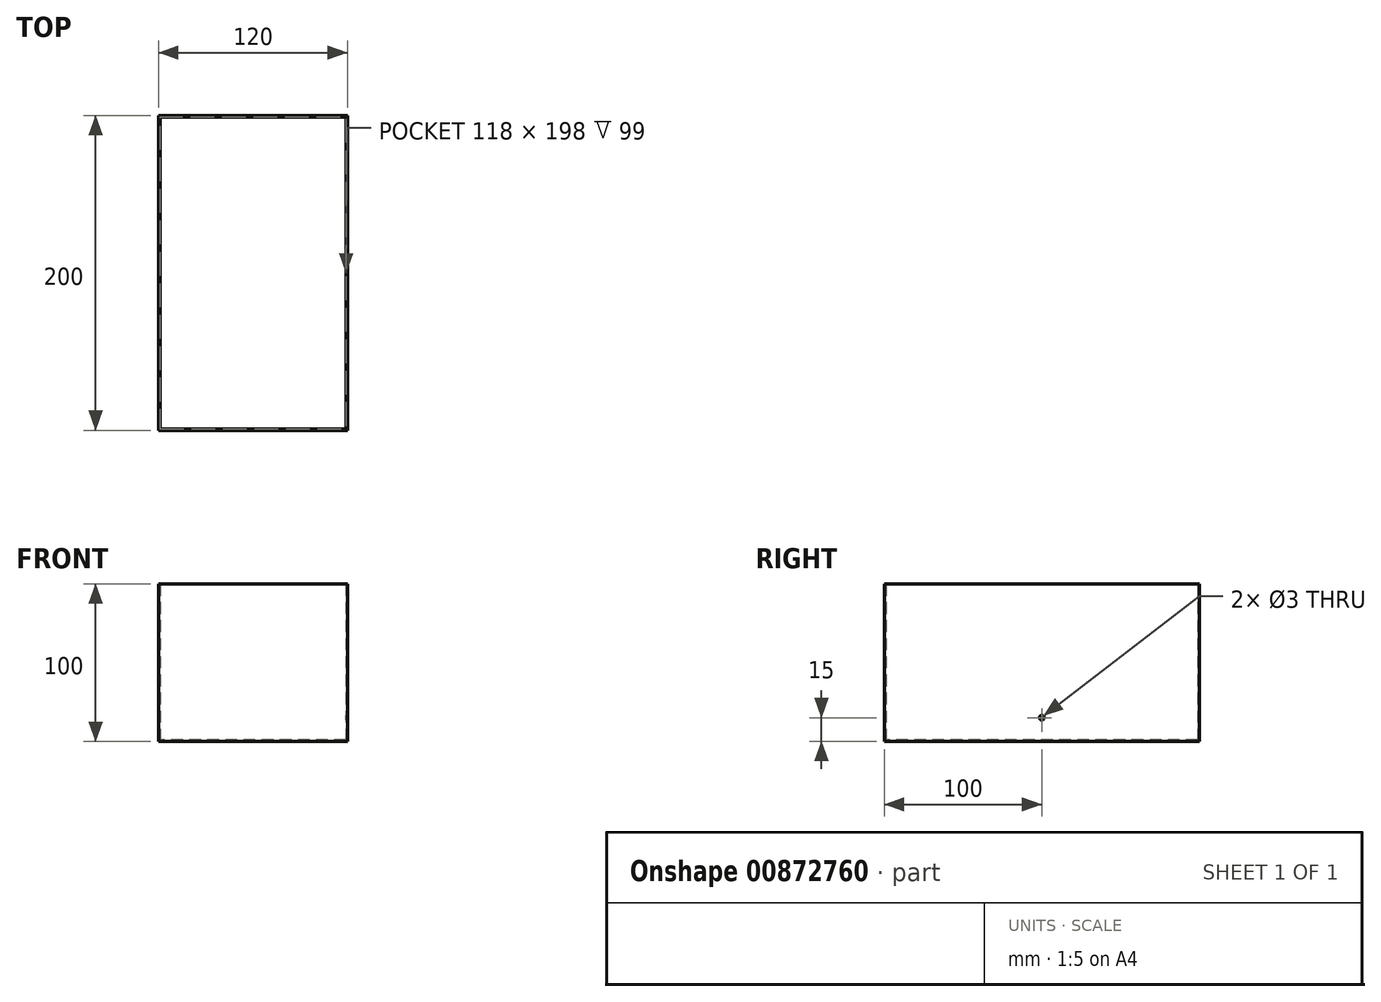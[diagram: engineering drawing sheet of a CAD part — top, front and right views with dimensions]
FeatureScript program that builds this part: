
annotation { "Feature Type Name" : "Feature", "Feature Type Description" : "" }
export const myFeature = defineFeature(function(context is Context, id is Id, definition is map)
    precondition{}
    {
        {
            var Q0;
            Q0=qCreatedBy(makeId("Top.planeOp"),FACE);
            var sketch = newSketch(context, id + "F0", { "sketchPlane" : qUnion([Q0])});
            skLineSegment(sketch, "E0.bottom", {"start": v(60, 100) * mm, "end": v(-60, 100) * mm});
            skLineSegment(sketch, "E0.top", {"start": v(60, -100) * mm, "end": v(-60, -100) * mm});
            skLineSegment(sketch, "E0.left", {"start": v(60, 100) * mm, "end": v(60, -100) * mm});
            skLineSegment(sketch, "E0.right", {"start": v(-60, 100) * mm, "end": v(-60, -100) * mm});
            skPoint(sketch, "E0.middle", {"position": v(0, 0) * mm});
            skSolve(sketch);
        }
        {
            var Q0;
            Q0=makeQuery(id+"F0.imprint","IMPRINT",FACE,{"disambiguationData":[TD([[makeQuery(id+"F0.imprint","IMPRINT",EDGE,{"derivedFrom":sQuery(id+"F0.wireOp",EDGE,"E0.bottom")}),1.0]])]});
            extrude(context, id + "F1", {"entities" : qUnion([Q0]), "depth" : 100 * mm, "offsetDistance" : 25 * mm});
        }
        {
            var Q0;
            Q0=makeQuery(id+"F1.opExtrude","CAP_FACE",FACE,{"disambiguationData":[OSD([sQuery(id+"F0.wireOp",EDGE,"E0.bottom"),sQuery(id+"F0.wireOp",EDGE,"E0.top"),sQuery(id+"F0.wireOp",EDGE,"E0.left"),sQuery(id+"F0.wireOp",EDGE,"E0.right")])],"isStart":false});
            shell(context, id + "F2", {"entities" : qUnion([Q0]), "thickness" : 1 * mm});
        }
        {
            var Q0;
            Q0=makeQuery(id+"F1.opExtrude","SWEPT_FACE",FACE,{"disambiguationData":[OSD([sQuery(id+"F0.wireOp",EDGE,"E0.right")])]});
            var sketch = newSketch(context, id + "F3", { "sketchPlane" : qUnion([Q0])});
            skLineSegment(sketch, "E1.0", {"start": v(-100, 100) * mm, "end": v(-100, 0) * mm});
            skLineSegment(sketch, "E2.0", {"start": v(100, 100) * mm, "end": v(100, 0) * mm});
            skLineSegment(sketch, "E3.0", {"start": v(-100, 0) * mm, "end": v(100, 0) * mm});
            skCircle(sketch, "E4", {"center": v(0, 15) * mm, "radius": 1.5 * mm});
            skSolve(sketch);
        }
        {
            var Q0;
            Q0=makeQuery(id+"F3.imprint","IMPRINT",FACE,{"disambiguationData":[TD([[makeQuery(id+"F3.imprint","IMPRINT",EDGE,{"derivedFrom":sQuery(id+"F3.wireOp",EDGE,"E4")}),1.0]])]});
            extrude(context, id + "F4", {"entities" : qUnion([Q0]), "operationType" : NewBodyOperationType.REMOVE, "oppositeDirection" : true, "depth" : 130 * mm, "offsetDistance" : 25 * mm});
        }
    });
